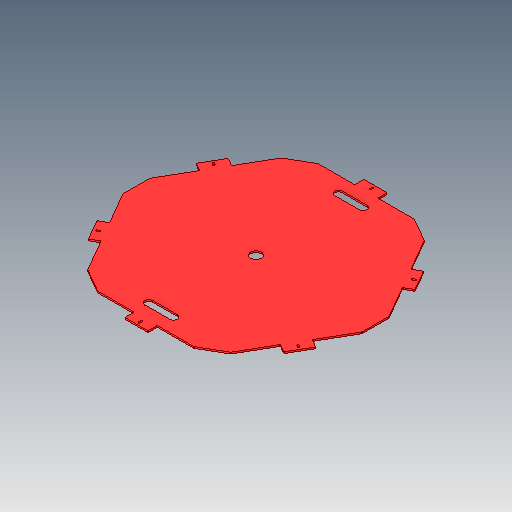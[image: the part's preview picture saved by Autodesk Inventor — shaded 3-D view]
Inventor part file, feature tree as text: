
AUTODESK INVENTOR PART (.ipt)
format: ipt  version: 2023.5 (Build 275446000, 446)  size: 167,424 bytes
history: native  units: in
note: dims shown in document units (in); Inventor stores cm internally (conversion verified against a paired STEP export)
features: fillet x1
ambient origin geometry x8: Origin, YZ Plane, XZ Plane, XY Plane, X Axis, Y Axis, Z Axis, Center Point
bodies: Solid1 (feature_tree)
feature tree (1):
  fillet  "Fillet2"  [1 undecoded]
note: 1 required parameter value undecoded (feature->parameter linkage not recoverable at this tier; creation-order binding heuristic only, values carry confidence <= 0.55)
